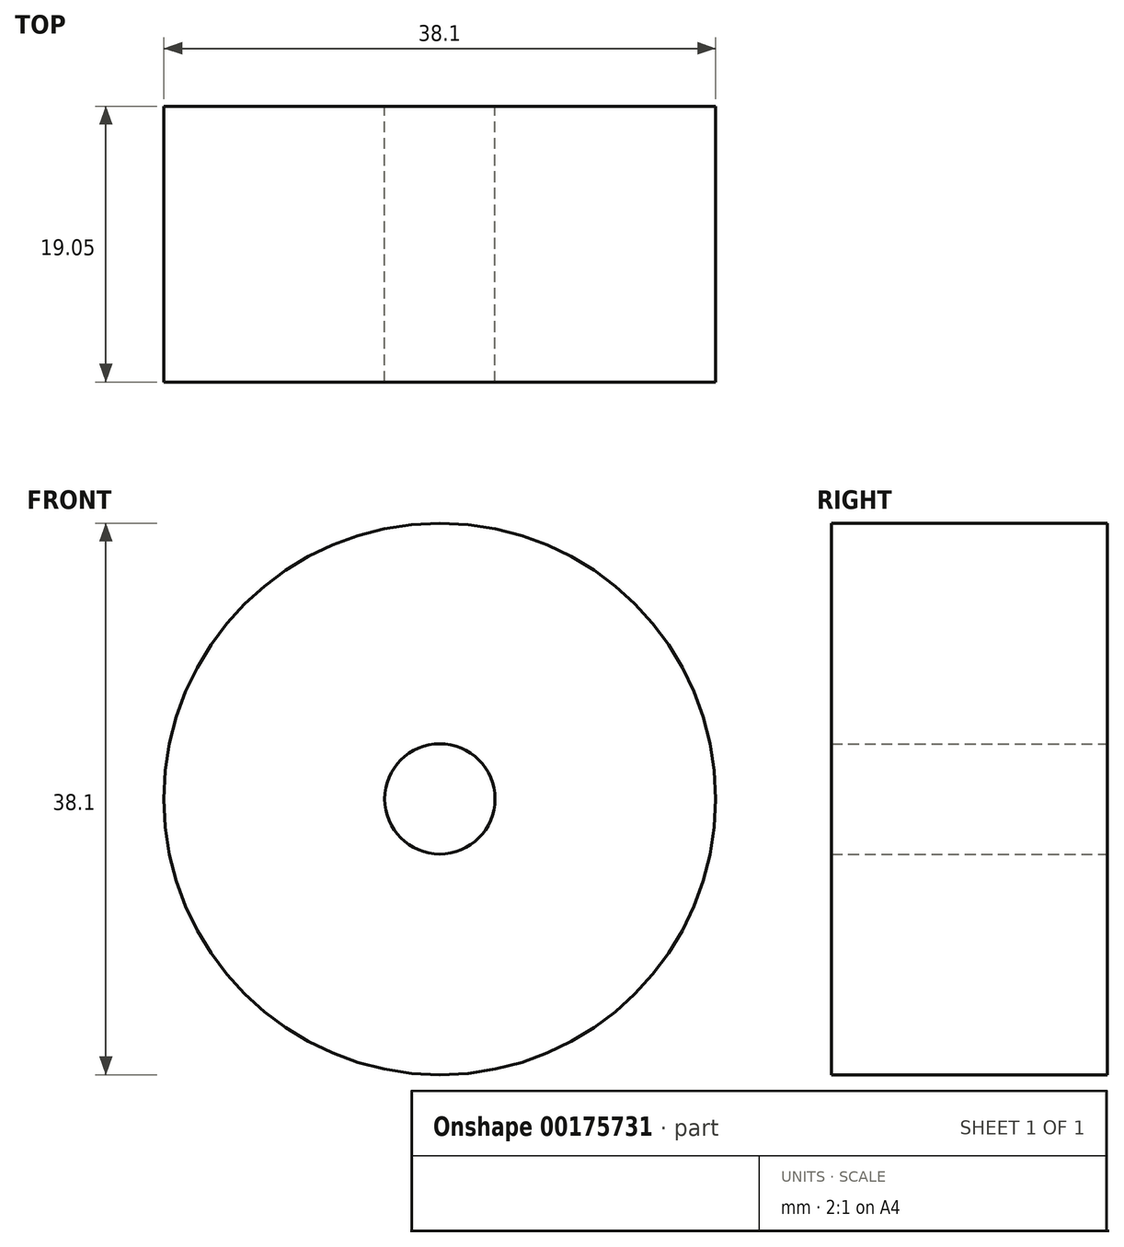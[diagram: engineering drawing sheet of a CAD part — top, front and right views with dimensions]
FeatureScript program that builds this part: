
annotation { "Feature Type Name" : "Feature", "Feature Type Description" : "" }
export const myFeature = defineFeature(function(context is Context, id is Id, definition is map)
    precondition{}
    {
        {
            var Q0;
            Q0=qCreatedBy(makeId("Front.planeOp"),FACE);
            var sketch = newSketch(context, id + "F0", { "sketchPlane" : qUnion([Q0])});
            skCircle(sketch, "E0", {"center": v(0, 0) * mm, "radius": 19.05 * mm});
            skCircle(sketch, "E1", {"center": v(0, 0) * mm, "radius": 3.81 * mm});
            skSolve(sketch);
        }
        {
            var Q0;
            Q0 = qSketchRegion(id + "F0", true);
            extrude(context, id + "F1", {"entities" : qUnion([Q0]), "depth" : 19.05 * mm});
        }
    });
